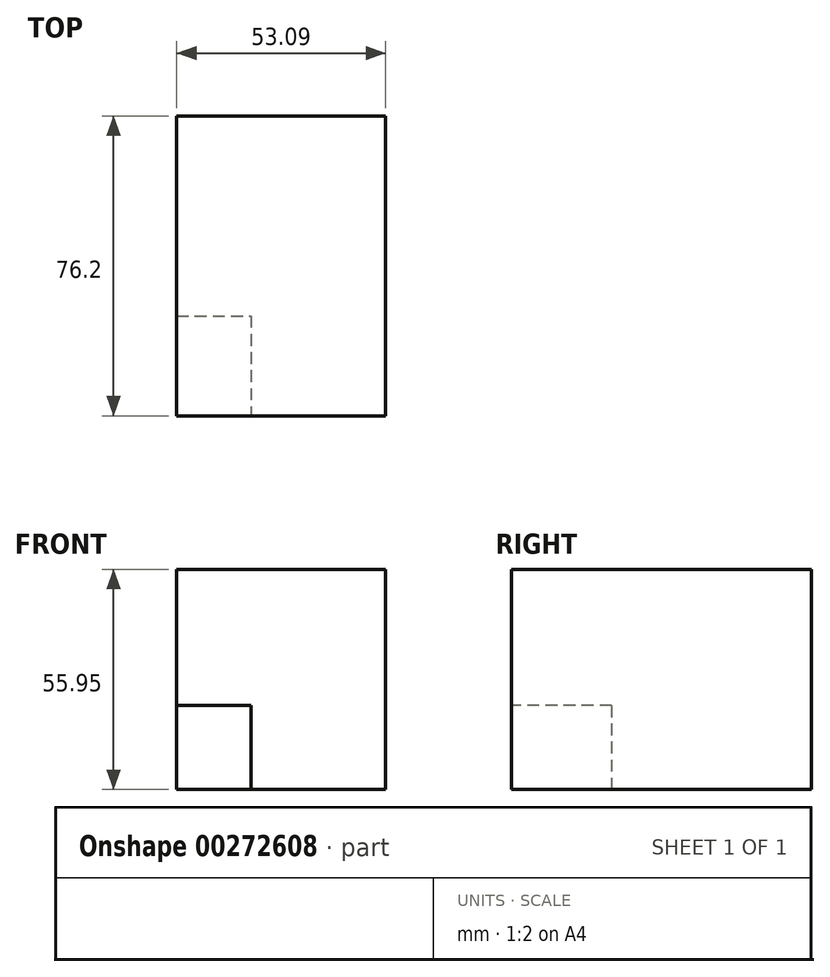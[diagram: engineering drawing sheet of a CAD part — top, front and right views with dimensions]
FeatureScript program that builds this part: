
annotation { "Feature Type Name" : "Feature", "Feature Type Description" : "" }
export const myFeature = defineFeature(function(context is Context, id is Id, definition is map)
    precondition{}
    {
        {
            var Q0;
            Q0=qCreatedBy(makeId("Front.planeOp"),FACE);
            var sketch = newSketch(context, id + "F0", { "sketchPlane" : qUnion([Q0])});
            skLineSegment(sketch, "E0", {"start": v(0, 55.95) * mm, "end": v(-53.09, 55.95) * mm});
            skLineSegment(sketch, "E1", {"start": v(-53.09, 55.95) * mm, "end": v(-53.09, 0) * mm});
            skLineSegment(sketch, "E2", {"start": v(-53.09, 0) * mm, "end": v(0, 0) * mm});
            skLineSegment(sketch, "E3", {"start": v(0, 0) * mm, "end": v(0, 55.95) * mm});
            skSolve(sketch);
        }
        {
            var Q0;
            Q0 = qSketchRegion(id + "F0", true);
            extrude(context, id + "F1", {"entities" : qUnion([Q0]), "depth" : 76.2 * mm});
        }
        {
            var Q0;
            Q0=makeQuery(id+"F1.opExtrude","CAP_FACE",FACE,{"disambiguationData":[OSD([sQuery(id+"F0.wireOp",EDGE,"E0"),sQuery(id+"F0.wireOp",EDGE,"E1"),sQuery(id+"F0.wireOp",EDGE,"E2"),sQuery(id+"F0.wireOp",EDGE,"E3")])],"isStart":false});
            var sketch = newSketch(context, id + "F2", { "sketchPlane" : qUnion([Q0])});
            skLineSegment(sketch, "E4", {"start": v(-53.09, 21.4) * mm, "end": v(-34.19, 21.4) * mm});
            skLineSegment(sketch, "E5", {"start": v(-34.19, 21.4) * mm, "end": v(-34.19, 0) * mm});
            skLineSegment(sketch, "E6", {"start": v(-53.09, 21.4) * mm, "end": v(-53.09, 0) * mm});
            skLineSegment(sketch, "E7", {"start": v(-53.09, 0) * mm, "end": v(-34.19, 0) * mm});
            skSolve(sketch);
        }
        {
            var Q0;
            Q0=makeQuery(id+"F2.imprint","IMPRINT",FACE,{"disambiguationData":[TD([[makeQuery(id+"F2.imprint","IMPRINT",EDGE,{"derivedFrom":sQuery(id+"F2.wireOp",EDGE,"E4")}),-1.0]])]});
            extrude(context, id + "F3", {"entities" : qUnion([Q0]), "operationType" : NewBodyOperationType.REMOVE, "oppositeDirection" : true, "depth" : 25.4 * mm});
        }
    });
